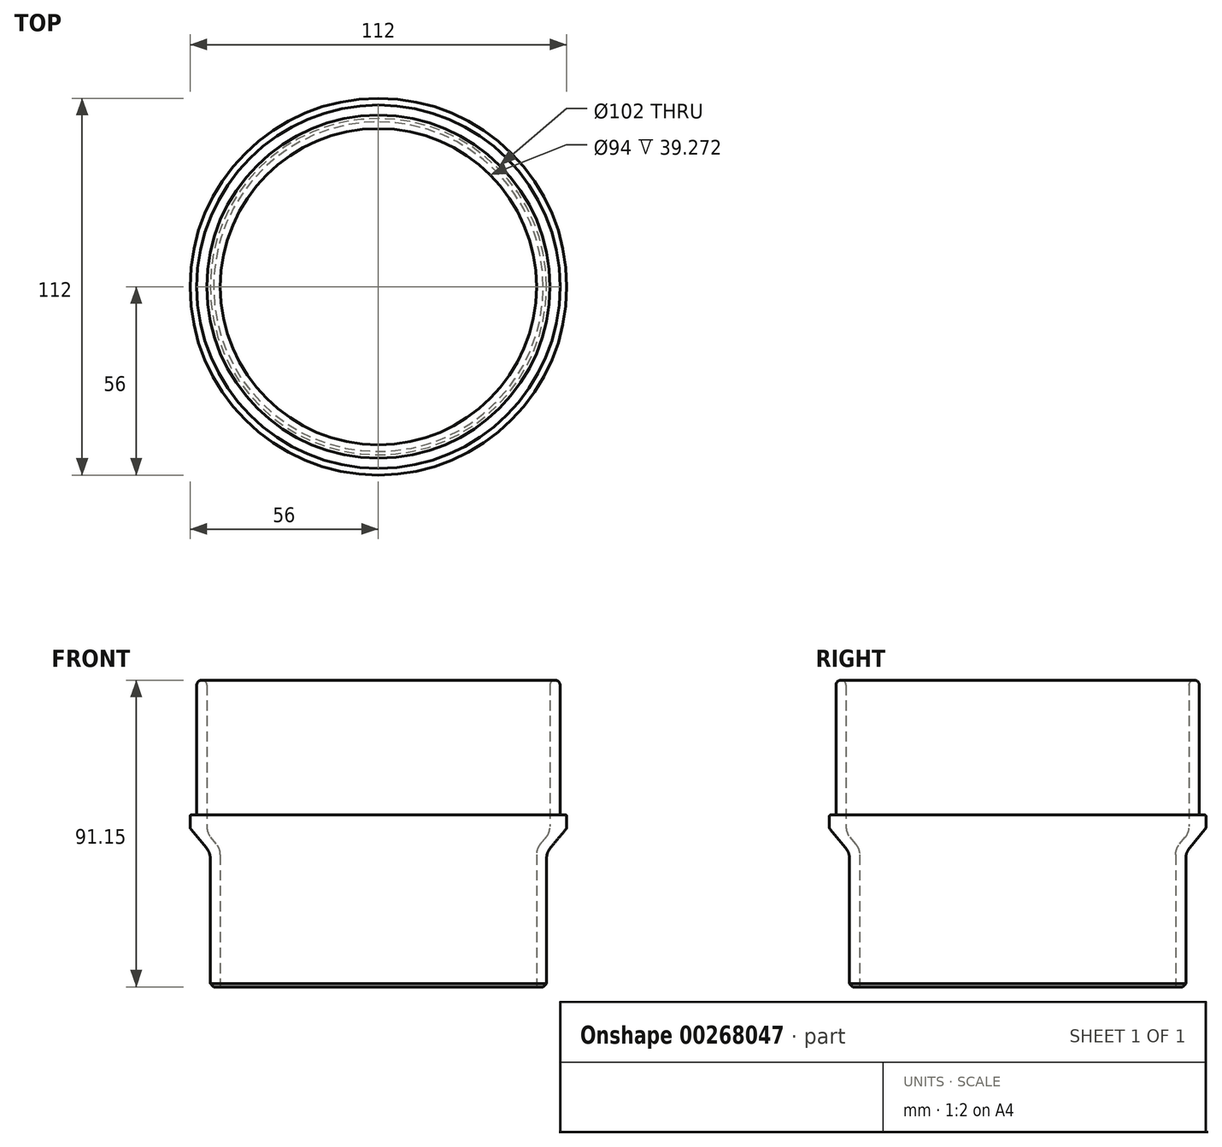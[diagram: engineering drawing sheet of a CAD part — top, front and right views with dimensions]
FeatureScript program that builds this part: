
annotation { "Feature Type Name" : "Feature", "Feature Type Description" : "" }
export const myFeature = defineFeature(function(context is Context, id is Id, definition is map)
    precondition{}
    {
        {
            var Q0;
            Q0=qCreatedBy(makeId("Front.planeOp"),FACE);
            var sketch = newSketch(context, id + "F0", { "sketchPlane" : qUnion([Q0])});
            skLineSegment(sketch, "E0", {"start": v(50, 0) * mm, "end": v(50, 40) * mm});
            skLineSegment(sketch, "E1", {"start": v(50, 40) * mm, "end": v(56, 47.15) * mm});
            skLineSegment(sketch, "E2", {"start": v(56, 47.15) * mm, "end": v(56, 51.15) * mm});
            skLineSegment(sketch, "E3", {"start": v(56, 51.15) * mm, "end": v(54, 51.15) * mm});
            skLineSegment(sketch, "E4", {"start": v(54, 51.15) * mm, "end": v(54, 91.15) * mm});
            skLineSegment(sketch, "E5", {"start": v(0, -37.25) * mm, "end": v(0, 130.62) * mm, "construction": true});
            skLineSegment(sketch, "E6", {"start": v(54, 91.15) * mm, "end": v(51, 91.15) * mm});
            skLineSegment(sketch, "E7", {"start": v(51, 91.15) * mm, "end": v(51, 45.86) * mm});
            skLineSegment(sketch, "E8", {"start": v(51, 45.86) * mm, "end": v(47, 41.1) * mm});
            skLineSegment(sketch, "E9", {"start": v(47, 41.1) * mm, "end": v(47, 0) * mm});
            skLineSegment(sketch, "E10", {"start": v(47, 0) * mm, "end": v(50, 0) * mm});
            skSolve(sketch);
        }
        {
            var Q0;
            Q0=makeQuery(id+"F0.imprint","IMPRINT",FACE,{"disambiguationData":[TD([[makeQuery(id+"F0.imprint","IMPRINT",EDGE,{"derivedFrom":sQuery(id+"F0.wireOp",EDGE,"E0")}),1.0]])]});
            var Q1;
            Q1=sQuery(id+"F0.wireOp",EDGE,"E5");
            revolve(context, id + "F1", {"entities" : qUnion([Q0]), "axis" : qUnion([Q1]), "revolveType" : RevolveType.FULL});
        }
        {
            var Q0;
            Q0=makeQuery(id+"F1.opRevolve","SWEPT_EDGE",EDGE,{"disambiguationData":[OSD([sQuery(id+"F0.wireOp",EDGE,"E4"),sQuery(id+"F0.wireOp",EDGE,"E6")])]});
            var Q1;
            Q1=makeQuery(id+"F1.opRevolve","SWEPT_EDGE",EDGE,{"disambiguationData":[OSD([sQuery(id+"F0.wireOp",EDGE,"E6"),sQuery(id+"F0.wireOp",EDGE,"E7")])]});
            var Q2;
            Q2=makeQuery(id+"F1.opRevolve","SWEPT_EDGE",EDGE,{"disambiguationData":[OSD([sQuery(id+"F0.wireOp",EDGE,"E1"),sQuery(id+"F0.wireOp",EDGE,"E2")])]});
            fillet(context, id + "F2", {"entities" : qUnion([Q0, Q1, Q2]), "radius" : 1.4 * mm, "tangentPropagation" : true, "allowEdgeOverflow" : false});
        }
        {
            var Q0;
            Q0=makeQuery(id+"F1.opRevolve","SWEPT_EDGE",EDGE,{"disambiguationData":[OSD([sQuery(id+"F0.wireOp",EDGE,"E2"),sQuery(id+"F0.wireOp",EDGE,"E3")])]});
            var Q1;
            Q1=makeQuery(id+"F1.opRevolve","SWEPT_EDGE",EDGE,{"disambiguationData":[OSD([sQuery(id+"F0.wireOp",EDGE,"E3"),sQuery(id+"F0.wireOp",EDGE,"E4")])]});
            fillet(context, id + "F3", {"entities" : qUnion([Q0, Q1]), "radius" : 0.5 * mm, "tangentPropagation" : true, "allowEdgeOverflow" : false});
        }
        {
            var Q0;
            Q0=makeQuery(id+"F1.opRevolve","SWEPT_EDGE",EDGE,{"disambiguationData":[OSD([sQuery(id+"F0.wireOp",EDGE,"E0"),sQuery(id+"F0.wireOp",EDGE,"E1")])]});
            var Q1;
            Q1=makeQuery(id+"F1.opRevolve","SWEPT_EDGE",EDGE,{"disambiguationData":[OSD([sQuery(id+"F0.wireOp",EDGE,"E8"),sQuery(id+"F0.wireOp",EDGE,"E9")])]});
            var Q2;
            Q2=makeQuery(id+"F1.opRevolve","SWEPT_EDGE",EDGE,{"disambiguationData":[OSD([sQuery(id+"F0.wireOp",EDGE,"E7"),sQuery(id+"F0.wireOp",EDGE,"E8")])]});
            fillet(context, id + "F4", {"entities" : qUnion([Q0, Q1, Q2]), "radius" : 5 * mm, "tangentPropagation" : true, "allowEdgeOverflow" : false});
        }
        {
            var Q0;
            Q0=makeQuery(id+"F1.opRevolve","SWEPT_EDGE",EDGE,{"disambiguationData":[OSD([sQuery(id+"F0.wireOp",EDGE,"E0"),sQuery(id+"F0.wireOp",EDGE,"E10")])]});
            chamfer(context, id + "F5", {"entities" : qUnion([Q0]), "width" : 1 * mm, "tangentPropagation" : true});
        }
    });
